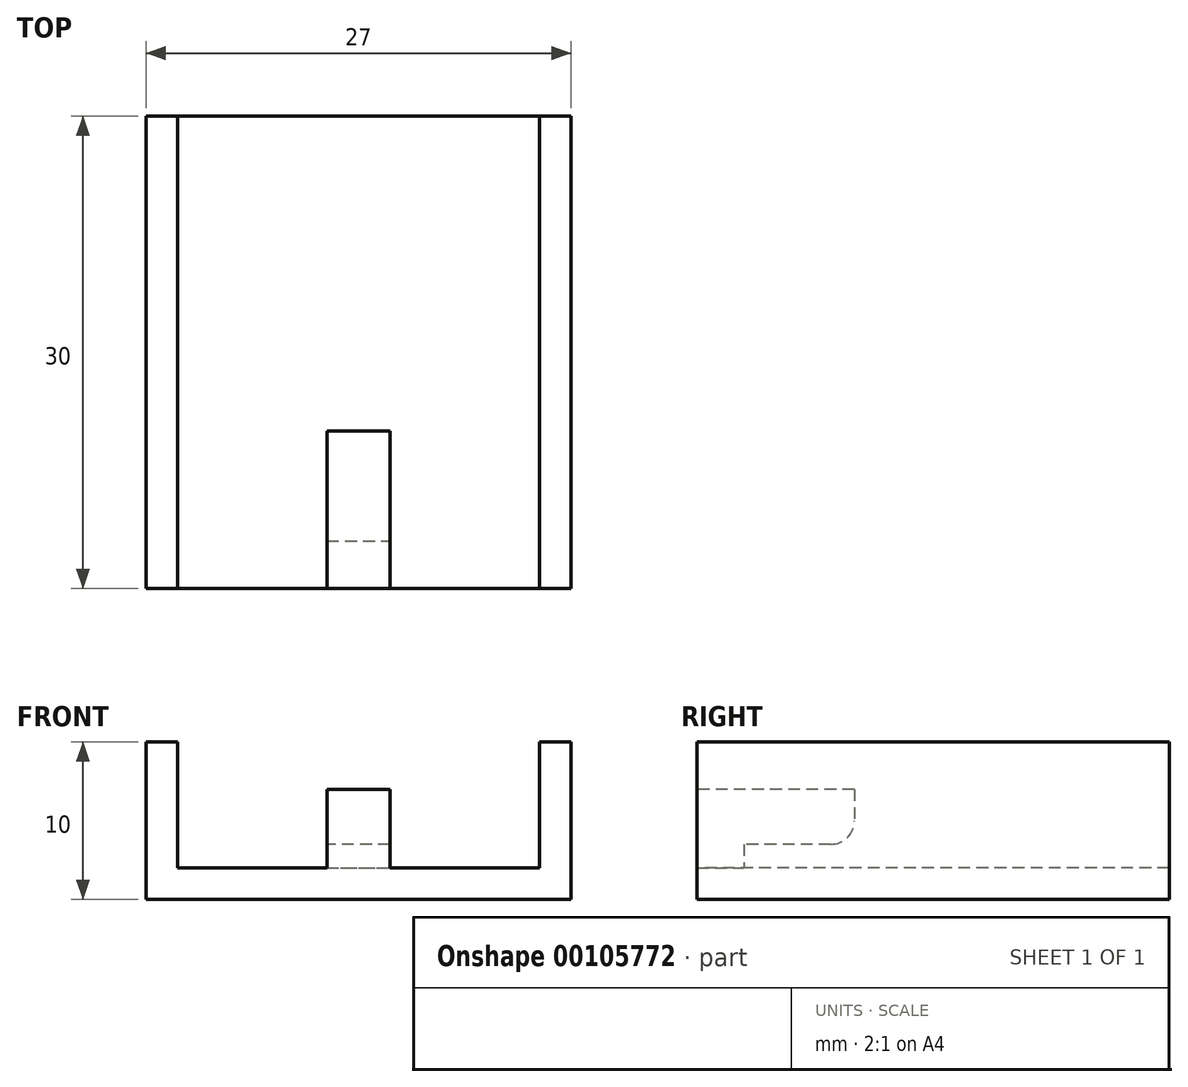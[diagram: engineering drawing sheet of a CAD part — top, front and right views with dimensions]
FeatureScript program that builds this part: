
annotation { "Feature Type Name" : "Feature", "Feature Type Description" : "" }
export const myFeature = defineFeature(function(context is Context, id is Id, definition is map)
    precondition{}
    {
        {
            var Q0;
            Q0=qCreatedBy(makeId("Top.planeOp"),FACE);
            var sketch = newSketch(context, id + "F0", { "sketchPlane" : qUnion([Q0])});
            skLineSegment(sketch, "E0.bottom", {"start": v(-13.5, 17.5) * mm, "end": v(13.5, 17.5) * mm});
            skLineSegment(sketch, "E0.top", {"start": v(-13.5, -17.5) * mm, "end": v(13.5, -17.5) * mm});
            skLineSegment(sketch, "E0.left", {"start": v(-13.5, 17.5) * mm, "end": v(-13.5, -17.5) * mm});
            skLineSegment(sketch, "E0.right", {"start": v(13.5, 17.5) * mm, "end": v(13.5, -17.5) * mm});
            skPoint(sketch, "E0.middle", {"position": v(0, 0) * mm});
            skLineSegment(sketch, "E1", {"start": v(-11.5, 17.5) * mm, "end": v(-11.5, -17.5) * mm});
            skLineSegment(sketch, "E2", {"start": v(11.5, 17.5) * mm, "end": v(11.5, -17.5) * mm});
            skLineSegment(sketch, "E3", {"start": v(-2, -17.5) * mm, "end": v(-2, -22.5) * mm});
            skLineSegment(sketch, "E4", {"start": v(-2, -22.5) * mm, "end": v(2, -22.5) * mm});
            skLineSegment(sketch, "E5", {"start": v(2, -22.5) * mm, "end": v(2, -17.5) * mm});
            skSolve(sketch);
        }
        {
            var Q0;
            {var subQ0=sQuery(id+"F0.wireOp",EDGE,"E1");Q0=makeQuery(id+"F0.imprint","IMPRINT",FACE,{"disambiguationData":[TD([[makeQuery(id+"F0.imprint","IMPRINT",EDGE,{"derivedFrom":subQ0}),1.0]])]});}
            extrude(context, id + "F1", {"entities" : qUnion([Q0]), "depth" : 2 * mm});
        }
        {
            var Q0;
            {var subQ0=sQuery(id+"F0.wireOp",EDGE,"E0.left");Q0=makeQuery(id+"F0.imprint","IMPRINT",FACE,{"disambiguationData":[TD([[makeQuery(id+"F0.imprint","IMPRINT",EDGE,{"derivedFrom":subQ0}),1.0]])]});}
            var Q1;
            {var subQ0=sQuery(id+"F0.wireOp",EDGE,"E0.right");Q1=makeQuery(id+"F0.imprint","IMPRINT",FACE,{"disambiguationData":[TD([[makeQuery(id+"F0.imprint","IMPRINT",EDGE,{"derivedFrom":subQ0}),-1.0]])]});}
            extrude(context, id + "F2", {"entities" : qUnion([Q0, Q1]), "operationType" : NewBodyOperationType.ADD, "depth" : 10 * mm});
        }
        {
            var Q0;
            {var subQ0=sQuery(id+"F0.wireOp",EDGE,"E3");Q0=makeQuery(id+"F0.imprint","IMPRINT",FACE,{"disambiguationData":[TD([[makeQuery(id+"F0.imprint","IMPRINT",EDGE,{"derivedFrom":subQ0}),1.0]])]});}
            extrude(context, id + "F3", {"entities" : qUnion([Q0]), "operationType" : NewBodyOperationType.ADD, "depth" : 7 * mm});
        }
        {
            var Q0;
            Q0=makeQuery(id+"F3.opExtrude","SWEPT_FACE",FACE,{"disambiguationData":[OSD([sQuery(id+"F0.wireOp",EDGE,"E0.top")])]});
            var sketch = newSketch(context, id + "F4", { "sketchPlane" : qUnion([Q0])});
            skLineSegment(sketch, "E6", {"start": v(-2, 3.5) * mm, "end": v(2, 3.5) * mm});
            skSolve(sketch);
        }
        {
            var Q0;
            {var subQ0=sQuery(id+"F4.wireOp",EDGE,"E6");Q0=makeQuery(id+"F4.imprint","IMPRINT",FACE,{"disambiguationData":[TD([[makeQuery(id+"F4.imprint","IMPRINT",EDGE,{"derivedFrom":subQ0}),1.0]])]});}
            extrude(context, id + "F5", {"entities" : qUnion([Q0]), "operationType" : NewBodyOperationType.ADD, "depth" : 5 * mm});
        }
        {
            var Q0;
            Q0=makeQuery(id+"F5.opExtrude","CAP_EDGE",EDGE,{"disambiguationData":[OSD([sQuery(id+"F4.wireOp",EDGE,"E6")])],"isStart":false});
            fillet(context, id + "F6", {"entities" : qUnion([Q0]), "radius" : 1.5 * mm, "tangentPropagation" : true, "allowEdgeOverflow" : false});
        }
        {
            var Q0;
            Q0=makeQuery(id+"F3.opExtrude","SWEPT_FACE",FACE,{"disambiguationData":[OSD([sQuery(id+"F0.wireOp",EDGE,"E0.top")])]});
            extrude(context, id + "F7", {"entities" : qUnion([Q0]), "operationType" : NewBodyOperationType.REMOVE, "oppositeDirection" : true, "depth" : 2 * mm});
        }
        {
            var Q0;
            {var subQ0=sQuery(id+"F0.wireOp",EDGE,"E0.bottom");Q0=makeQuery(id+"F2.boolean.opBoolean","MERGE",FACE,{"derivedFrom":[makeQuery(id+"F1.opExtrude","SWEPT_FACE",FACE,{"disambiguationData":[OSD([subQ0])]}),makeQuery(id+"F2.opExtrude","SWEPT_FACE",FACE,{"disambiguationData":[OSD([subQ0]),TDD([makeQuery(id+"F0.imprint","IMPRINT",EDGE,{"disambiguationData":[TD([[makeQuery(id+"F0.imprint","INTERSECT",VERTEX,{"derivedFrom":[subQ0,sQuery(id+"F0.wireOp",EDGE,"E0.left")]}),-1.0]])],"derivedFrom":subQ0})])]}),makeQuery(id+"F2.opExtrude","SWEPT_FACE",FACE,{"disambiguationData":[OSD([subQ0]),TDD([makeQuery(id+"F0.imprint","IMPRINT",EDGE,{"disambiguationData":[TD([[makeQuery(id+"F0.imprint","INTERSECT",VERTEX,{"derivedFrom":[subQ0,sQuery(id+"F0.wireOp",EDGE,"E0.right")]}),1.0]])],"derivedFrom":subQ0})])]})]});}
            extrude(context, id + "F8", {"entities" : qUnion([Q0]), "operationType" : NewBodyOperationType.REMOVE, "oppositeDirection" : true, "depth" : 5 * mm});
        }
        {
            var Q0;
            {var subQ1=sQuery(id+"F0.wireOp",EDGE,"E0.left");var subQ2=sQuery(id+"F0.wireOp",EDGE,"E0.top");var subQ5=sQuery(id+"F0.wireOp",EDGE,"E0.right");Q0=makeQuery(id+"F3.boolean.opBoolean","SPLIT",FACE,{"disambiguationData":[TD([makeQuery(id+"F2.opExtrude","SWEPT_FACE",FACE,{"disambiguationData":[OSD([subQ5])]})])],"derivedFrom":makeQuery(id+"F2.boolean.opBoolean","MERGE",FACE,{"derivedFrom":[makeQuery(id+"F1.opExtrude","SWEPT_FACE",FACE,{"disambiguationData":[OSD([subQ2])]}),makeQuery(id+"F2.opExtrude","SWEPT_FACE",FACE,{"disambiguationData":[OSD([subQ2]),TDD([makeQuery(id+"F0.imprint","IMPRINT",EDGE,{"disambiguationData":[TD([[makeQuery(id+"F0.imprint","INTERSECT",VERTEX,{"derivedFrom":[subQ2,subQ1]}),-1.0]])],"derivedFrom":subQ2})])]}),makeQuery(id+"F2.opExtrude","SWEPT_FACE",FACE,{"disambiguationData":[OSD([subQ2]),TDD([makeQuery(id+"F0.imprint","IMPRINT",EDGE,{"disambiguationData":[TD([[makeQuery(id+"F0.imprint","INTERSECT",VERTEX,{"derivedFrom":[subQ2,subQ5]}),1.0]])],"derivedFrom":subQ2})])]})]})});}
            var Q1;
            {var subQ1=sQuery(id+"F0.wireOp",EDGE,"E0.left");var subQ2=sQuery(id+"F0.wireOp",EDGE,"E0.top");var subQ5=sQuery(id+"F0.wireOp",EDGE,"E0.right");Q1=makeQuery(id+"F3.boolean.opBoolean","SPLIT",FACE,{"disambiguationData":[TD([makeQuery(id+"F2.opExtrude","SWEPT_FACE",FACE,{"disambiguationData":[OSD([subQ1])]})])],"derivedFrom":makeQuery(id+"F2.boolean.opBoolean","MERGE",FACE,{"derivedFrom":[makeQuery(id+"F1.opExtrude","SWEPT_FACE",FACE,{"disambiguationData":[OSD([subQ2])]}),makeQuery(id+"F2.opExtrude","SWEPT_FACE",FACE,{"disambiguationData":[OSD([subQ2]),TDD([makeQuery(id+"F0.imprint","IMPRINT",EDGE,{"disambiguationData":[TD([[makeQuery(id+"F0.imprint","INTERSECT",VERTEX,{"derivedFrom":[subQ2,subQ1]}),-1.0]])],"derivedFrom":subQ2})])]}),makeQuery(id+"F2.opExtrude","SWEPT_FACE",FACE,{"disambiguationData":[OSD([subQ2]),TDD([makeQuery(id+"F0.imprint","IMPRINT",EDGE,{"disambiguationData":[TD([[makeQuery(id+"F0.imprint","INTERSECT",VERTEX,{"derivedFrom":[subQ2,subQ5]}),1.0]])],"derivedFrom":subQ2})])]})]})});}
            var Q2;
            {var subQ1=sQuery(id+"F0.wireOp",EDGE,"E0.left");var subQ2=sQuery(id+"F0.wireOp",EDGE,"E0.top");var subQ5=sQuery(id+"F0.wireOp",EDGE,"E0.right");Q2=makeQuery(id+"F3.boolean.opBoolean","SPLIT",FACE,{"disambiguationData":[TD([makeQuery(id+"F2.opExtrude","SWEPT_FACE",FACE,{"disambiguationData":[OSD([subQ1])]})])],"derivedFrom":makeQuery(id+"F2.boolean.opBoolean","MERGE",FACE,{"derivedFrom":[makeQuery(id+"F1.opExtrude","SWEPT_FACE",FACE,{"disambiguationData":[OSD([subQ2])]}),makeQuery(id+"F2.opExtrude","SWEPT_FACE",FACE,{"disambiguationData":[OSD([subQ2]),TDD([makeQuery(id+"F0.imprint","IMPRINT",EDGE,{"disambiguationData":[TD([[makeQuery(id+"F0.imprint","INTERSECT",VERTEX,{"derivedFrom":[subQ2,subQ1]}),-1.0]])],"derivedFrom":subQ2})])]}),makeQuery(id+"F2.opExtrude","SWEPT_FACE",FACE,{"disambiguationData":[OSD([subQ2]),TDD([makeQuery(id+"F0.imprint","IMPRINT",EDGE,{"disambiguationData":[TD([[makeQuery(id+"F0.imprint","INTERSECT",VERTEX,{"derivedFrom":[subQ2,subQ5]}),1.0]])],"derivedFrom":subQ2})])]})]})});}
            extrude(context, id + "F9", {"entities" : qUnion([Q0, Q1]), "operationType" : NewBodyOperationType.ADD, "endBoundEntityFace" : qUnion([Q2]), "depth" : 5 * mm});
        }
        {
            var Q0;
            Q0=makeQuery(id+"F8.boolean.opBoolean","COPY",FACE,{"derivedFrom":makeQuery(id+"F8.opExtrude","CAP_FACE",FACE,{"disambiguationData":[OSD([sQuery(id+"F0.wireOp",EDGE,"E0.bottom")])],"isStart":false})});
            extrude(context, id + "F10", {"entities" : qUnion([Q0]), "operationType" : NewBodyOperationType.REMOVE, "oppositeDirection" : true, "depth" : 5 * mm});
        }
    });
